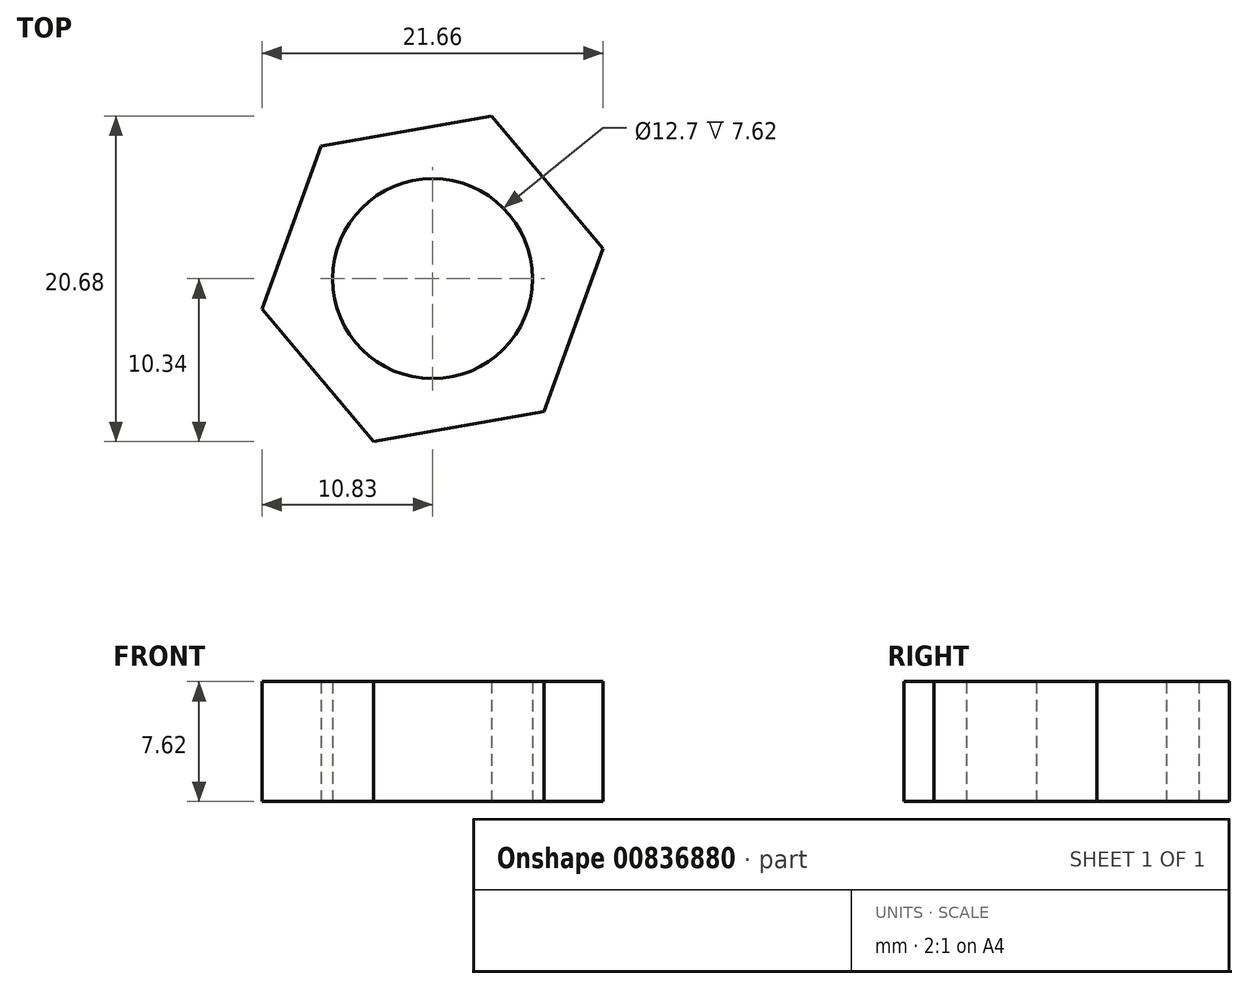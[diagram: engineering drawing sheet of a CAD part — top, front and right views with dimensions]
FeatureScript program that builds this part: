
annotation { "Feature Type Name" : "Feature", "Feature Type Description" : "" }
export const myFeature = defineFeature(function(context is Context, id is Id, definition is map)
    precondition{}
    {
        {
            var Q0;
            Q0=qCreatedBy(makeId("Top.planeOp"),FACE);
            var sketch = newSketch(context, id + "F0", { "sketchPlane" : qUnion([Q0])});
            skCircle(sketch, "E0.cCircle", {"center": v(0, 0) * mm, "radius": 9.53 * mm, "construction": true});
            skLineSegment(sketch, "E0.0", {"start": v(3.76, 10.34) * mm, "end": v(10.83, 1.92) * mm});
            skLineSegment(sketch, "E0.1", {"start": v(10.83, 1.92) * mm, "end": v(7.08, -8.42) * mm});
            skLineSegment(sketch, "E0.2", {"start": v(7.08, -8.42) * mm, "end": v(-3.76, -10.34) * mm});
            skLineSegment(sketch, "E0.3", {"start": v(-3.76, -10.34) * mm, "end": v(-10.83, -1.92) * mm});
            skLineSegment(sketch, "E0.4", {"start": v(-10.83, -1.92) * mm, "end": v(-7.08, 8.42) * mm});
            skLineSegment(sketch, "E0.5", {"start": v(-7.08, 8.42) * mm, "end": v(3.76, 10.34) * mm});
            skPoint(sketch, "E0.0.midPoint", {"position": v(7.3, 6.13) * mm});
            skCircle(sketch, "E1", {"center": v(0, 0) * mm, "radius": 6.35 * mm});
            skSolve(sketch);
        }
        {
            var Q0;
            Q0 = qSketchRegion(id + "F0", true);
            extrude(context, id + "F1", {"entities" : qUnion([Q0]), "depth" : 7.62 * mm, "offsetDistance" : 25.4 * mm});
        }
    });
